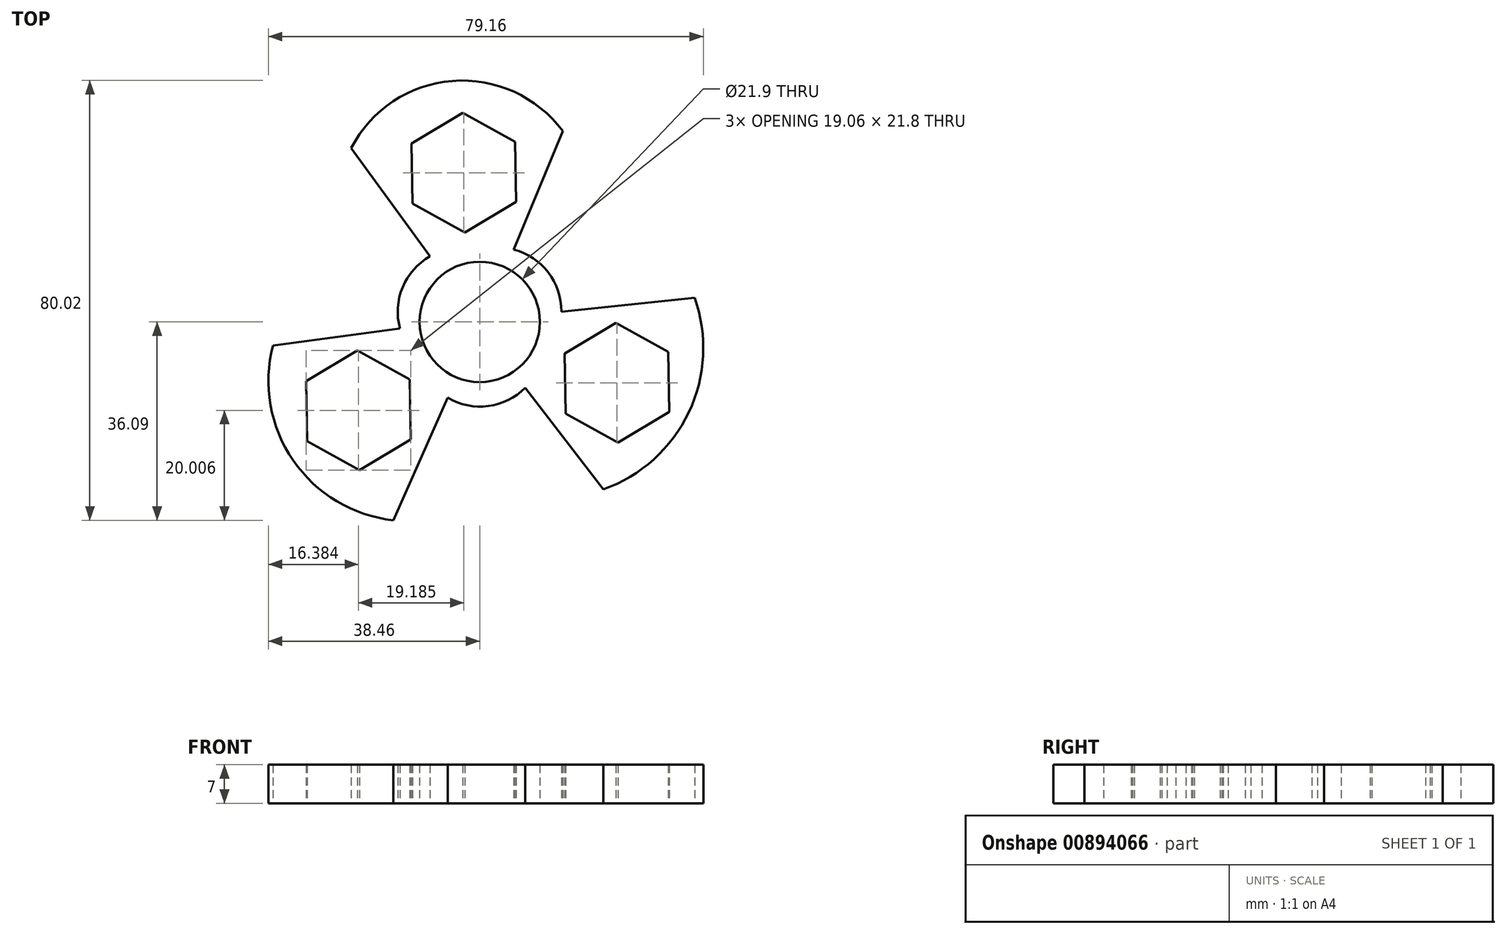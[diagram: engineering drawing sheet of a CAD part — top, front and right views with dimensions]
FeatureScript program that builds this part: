
annotation { "Feature Type Name" : "Feature", "Feature Type Description" : "" }
export const myFeature = defineFeature(function(context is Context, id is Id, definition is map)
    precondition{}
    {
        {
            var Q0;
            Q0=qCreatedBy(makeId("Top.planeOp"),FACE);
            var sketch = newSketch(context, id + "F0", { "sketchPlane" : qUnion([Q0])});
            skCircle(sketch, "E0", {"center": v(0, 0) * mm, "radius": 10.95 * mm});
            skCircle(sketch, "E1.cCircle", {"center": v(-2.9, 27.16) * mm, "radius": 9.44 * mm, "construction": true});
            skLineSegment(sketch, "E1.0", {"start": v(6.64, 21.87) * mm, "end": v(-2.7, 16.26) * mm});
            skLineSegment(sketch, "E1.1", {"start": v(-2.7, 16.26) * mm, "end": v(-12.24, 21.55) * mm});
            skLineSegment(sketch, "E1.2", {"start": v(-12.24, 21.55) * mm, "end": v(-12.42, 32.45) * mm});
            skLineSegment(sketch, "E1.3", {"start": v(-12.42, 32.45) * mm, "end": v(-3.07, 38.06) * mm});
            skLineSegment(sketch, "E1.4", {"start": v(-3.07, 38.06) * mm, "end": v(6.46, 32.77) * mm});
            skLineSegment(sketch, "E1.5", {"start": v(6.46, 32.77) * mm, "end": v(6.64, 21.87) * mm});
            skPoint(sketch, "E1.0.midPoint", {"position": v(1.97, 19.07) * mm});
            skLineSegment(sketch, "E2.1.0", {"start": v(-21.9, -26.98) * mm, "end": v(-31.42, -21.7) * mm});
            skLineSegment(sketch, "E2.1.1", {"start": v(-31.42, -21.7) * mm, "end": v(-31.6, -10.8) * mm});
            skCircle(sketch, "E2.1.2", {"center": v(-22.08, -16.08) * mm, "radius": 9.44 * mm, "construction": true});
            skLineSegment(sketch, "E2.1.3", {"start": v(-31.6, -10.8) * mm, "end": v(-22.26, -5.19) * mm});
            skLineSegment(sketch, "E2.1.4", {"start": v(-22.26, -5.19) * mm, "end": v(-12.73, -10.48) * mm});
            skLineSegment(sketch, "E2.1.5", {"start": v(-12.73, -10.48) * mm, "end": v(-12.55, -21.37) * mm});
            skLineSegment(sketch, "E2.1.6", {"start": v(-12.55, -21.37) * mm, "end": v(-21.9, -26.98) * mm});
            skLineSegment(sketch, "E2.2.0", {"start": v(34.31, -5.47) * mm, "end": v(34.5, -16.37) * mm});
            skLineSegment(sketch, "E2.2.1", {"start": v(34.5, -16.37) * mm, "end": v(25.15, -21.98) * mm});
            skCircle(sketch, "E2.2.2", {"center": v(24.97, -11.08) * mm, "radius": 9.44 * mm, "construction": true});
            skLineSegment(sketch, "E2.2.3", {"start": v(25.15, -21.98) * mm, "end": v(15.62, -16.68) * mm});
            skLineSegment(sketch, "E2.2.4", {"start": v(15.62, -16.68) * mm, "end": v(15.44, -5.79) * mm});
            skLineSegment(sketch, "E2.2.5", {"start": v(15.44, -5.79) * mm, "end": v(24.78, -0.18) * mm});
            skLineSegment(sketch, "E2.2.6", {"start": v(24.78, -0.18) * mm, "end": v(34.31, -5.47) * mm});
            skArc(sketch, "E3", {"start": v(-9.03, 11.94) * mm, "mid": v(-14.04, 6.3) * mm, "end": v(-14.51, -1.21) * mm});
            skArc(sketch, "E4.1.0", {"start": v(-5.82, -13.8) * mm, "mid": v(1.56, -15.3) * mm, "end": v(8.3, -11.96) * mm});
            skArc(sketch, "E4.2.0", {"start": v(14.85, 1.86) * mm, "mid": v(12.48, 9) * mm, "end": v(6.2, 13.18) * mm});
            skLineSegment(sketch, "E5", {"start": v(-9.03, 11.94) * mm, "end": v(-23.39, 31.66) * mm});
            skLineSegment(sketch, "E6", {"start": v(-14.51, -1.21) * mm, "end": v(-37.63, -4.28) * mm});
            skLineSegment(sketch, "E7.1.0", {"start": v(-5.82, -13.8) * mm, "end": v(-15.72, -36.09) * mm});
            skLineSegment(sketch, "E7.1.1", {"start": v(8.3, -11.96) * mm, "end": v(22.53, -30.45) * mm});
            skLineSegment(sketch, "E7.2.0", {"start": v(14.85, 1.86) * mm, "end": v(39.11, 4.43) * mm});
            skLineSegment(sketch, "E7.2.1", {"start": v(6.2, 13.18) * mm, "end": v(15.1, 34.73) * mm});
            skArc(sketch, "E8", {"start": v(15.1, 34.73) * mm, "mid": v(-5, 43.86) * mm, "end": v(-23.39, 31.66) * mm});
            skArc(sketch, "E9", {"start": v(22.53, -30.45) * mm, "mid": v(38.05, -16.45) * mm, "end": v(39.11, 4.43) * mm});
            skArc(sketch, "E10", {"start": v(-37.63, -4.28) * mm, "mid": v(-33.95, -25.2) * mm, "end": v(-15.72, -36.09) * mm});
            skSolve(sketch);
        }
        {
            var Q0;
            Q0=makeQuery(id+"F0.imprint","IMPRINT",FACE,{"disambiguationData":[TD([[makeQuery(id+"F0.imprint","IMPRINT",EDGE,{"derivedFrom":sQuery(id+"F0.wireOp",EDGE,"E0")}),-1.0]])]});
            extrude(context, id + "F1", {"entities" : qUnion([Q0]), "depth" : 7 * mm, "offsetDistance" : 25 * mm});
        }
    });
